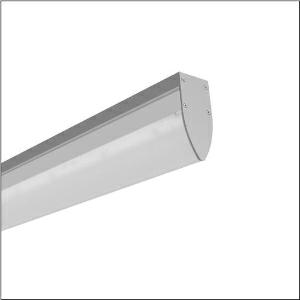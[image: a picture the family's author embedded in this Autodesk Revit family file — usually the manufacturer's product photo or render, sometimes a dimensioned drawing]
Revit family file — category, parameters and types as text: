
# Revit family: mira_r__21_td_51fr527d434a_4418
name_source: partatom
category: Lighting Fixtures
units: mm (PartAtom-declared; Revit-internal decimal feet)

## family parameters
Cut with Voids When Loaded = No
Host = Face
Light Source = No
Part Type = Normal
Room Calculation Point = No
Round Connector Dimension = Use Diameter
Shared = No

## types (1)
- Mira® 21 TD (1 x LED, 3660 lm, 26 W, 4000K)
    Apparent Load = 26 VA
    CIE Flux Codes = 40 68 87 81 100
    Color Rendering = 80
    Color Temperature = 4000K
    Default Elevation = 1800 mm
    Description = Mira® 21 TD, clean room luminaire, primary light control with reflector, primary optical cover: cover, of PMMA, frosted, light emission: direct distribution, primary light characteristic: symmetric, installation type: surface-mounted, LED, rated luminous flux: 3.660lm, luminous efficacy: 141lm/W, light colour: 840, colour temperature: 4000K, control gear: ECG, with terminal, 3-pole, max. 2.5mm², mains connection: 230V, AC, 50/60Hz, rated input power: 26W, luminaire housing, of sheet steel, coated, pure white (RAL 9010), length: 600mm, width: 55mm, height: 120mm, protection rating (complete): IP43, insulation class (complete): insulation class I (protective earthing), certification: CE, UKCA, permissible operating ambient temperature: -5..+40°C, standard: EN 50419, packaging unit: 1 piece
    Height = 0 mm  [stored 0 ft]
    Lamp = 1 x LED
    Lamp Light Flux = 3660 lm
    Lamp Power = 26 W
    Lamp count = 1
    Length = 600 mm
    Luminous efficacy = 141 lm/W
    Manufacturer = Siteco
    ModVariant = No
    Model = 51FR527D434A
    Mounting Place = Ceiling
    Mounting Type = Recessed
    Number of Poles = 1
    OnlyDefault = Yes
    Power Factor = 1
    Product Name = Mira® 21 TD
    Product group = clean room luminaire
    ProductGroupID = 402
    Protection Class = Protection class I
    Protection Degree = IP 43
    RLX_Detail_Level = 1
    RLX_Emergency_Light_Flux = 0 lm
    RLX_Emergency_Type = 0
    RLX_Emergency_Type_DB = No
    RlxData = <blob elided: 25909 chars, md5=fc49eacf>
    Socket = socket
    Standby Power = 0 W
    System Light Flux = 3660 lm
    System Power = 26 W
    Type Comments = Product without accessories
    Type Image = l_1007115.jpg
    URL = http://relux.com
    VarID = ---
    Voltage = 0 V
    Weight = 0.00 kg
    Width = 55 mm

note: [stored X ft] marks values corroborated as IEEE doubles in the binary element streams (Revit-internal decimal feet)

## geometry (parser evidence)
native form markers: Blend x4, Sweep x14
no freeform markers — native parametric forms only
